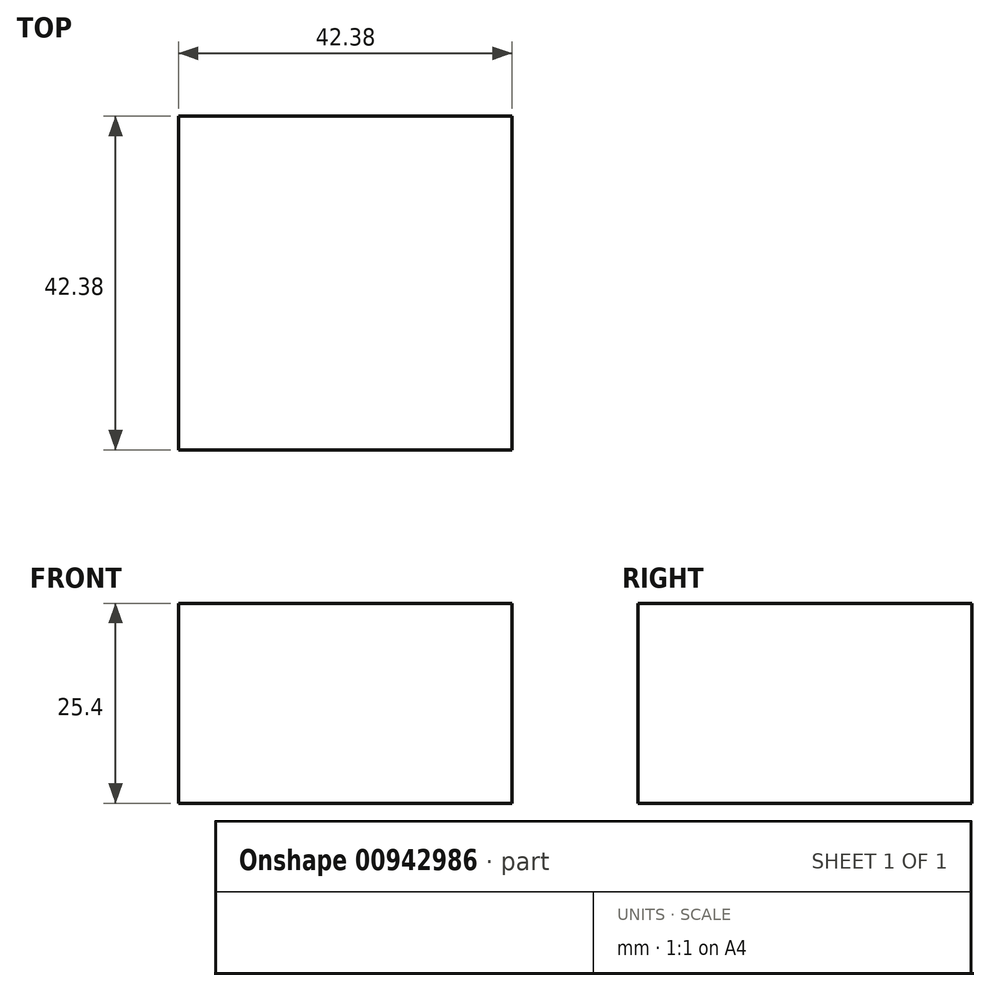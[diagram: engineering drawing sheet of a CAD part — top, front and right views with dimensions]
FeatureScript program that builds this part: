
annotation { "Feature Type Name" : "Feature", "Feature Type Description" : "" }
export const myFeature = defineFeature(function(context is Context, id is Id, definition is map)
    precondition{}
    {
        {
            var Q0;
            Q0=qCreatedBy(makeId("Top.planeOp"),FACE);
            var sketch = newSketch(context, id + "F0", { "sketchPlane" : qUnion([Q0])});
            skLineSegment(sketch, "E0.0", {"start": v(21.2, 21.2) * mm, "end": v(21.2, -21.2) * mm, "construction": true});
            skLineSegment(sketch, "E0.1", {"start": v(21.2, -21.2) * mm, "end": v(-21.2, -21.2) * mm});
            skLineSegment(sketch, "E0.2", {"start": v(-21.2, -21.2) * mm, "end": v(-21.2, 21.2) * mm});
            skLineSegment(sketch, "E0.3", {"start": v(-21.2, 21.2) * mm, "end": v(21.2, 21.2) * mm});
            skPoint(sketch, "E0.0.midPoint", {"position": v(21.2, 0) * mm});
            skLineSegment(sketch, "E1", {"start": v(21.2, -21.2) * mm, "end": v(21.2, 0) * mm});
            skLineSegment(sketch, "E2", {"start": v(21.2, 21.2) * mm, "end": v(21.2, 0) * mm});
            skLineSegment(sketch, "E3", {"start": v(0, -21.2) * mm, "end": v(-21.2, 0) * mm});
            skLineSegment(sketch, "E4", {"start": v(-21.2, 0) * mm, "end": v(0, 21.2) * mm});
            skLineSegment(sketch, "E5", {"start": v(0, 21.2) * mm, "end": v(21.2, 0) * mm});
            skLineSegment(sketch, "E6", {"start": v(21.2, 0) * mm, "end": v(0, -21.2) * mm});
            skLineSegment(sketch, "E7.top", {"start": v(-21.2, -21.2) * mm, "end": v(21.2, -21.2) * mm});
            skLineSegment(sketch, "E7.left", {"start": v(-21.2, 21.2) * mm, "end": v(-21.2, -21.2) * mm});
            skLineSegment(sketch, "E7.right", {"start": v(21.2, 21.2) * mm, "end": v(21.2, -21.2) * mm});
            skPoint(sketch, "E7.middle", {"position": v(0, 0) * mm});
            skSolve(sketch);
        }
        {
            var Q0;
            {var subQ0=sQuery(id+"F0.wireOp",EDGE,"E5");Q0=makeQuery(id+"F0.imprint","IMPRINT",FACE,{"disambiguationData":[TD([[makeQuery(id+"F0.imprint","IMPRINT",EDGE,{"derivedFrom":subQ0}),1.0]])]});}
            var Q1;
            Q1=makeQuery(id+"F0.imprint","IMPRINT",FACE,{"disambiguationData":[TD([[makeQuery(id+"F0.imprint","IMPRINT",EDGE,{"derivedFrom":sQuery(id+"F0.wireOp",EDGE,"E3")}),-1.0]])]});
            var Q2;
            {var subQ0=sQuery(id+"F0.wireOp",EDGE,"E3");Q2=makeQuery(id+"F0.imprint","IMPRINT",FACE,{"disambiguationData":[TD([[makeQuery(id+"F0.imprint","IMPRINT",EDGE,{"derivedFrom":subQ0}),1.0]])]});}
            var Q3;
            {var subQ0=sQuery(id+"F0.wireOp",EDGE,"E6");Q3=makeQuery(id+"F0.imprint","IMPRINT",FACE,{"disambiguationData":[TD([[makeQuery(id+"F0.imprint","IMPRINT",EDGE,{"derivedFrom":subQ0}),1.0]])]});}
            var Q4;
            {var subQ0=sQuery(id+"F0.wireOp",EDGE,"E4");Q4=makeQuery(id+"F0.imprint","IMPRINT",FACE,{"disambiguationData":[TD([[makeQuery(id+"F0.imprint","IMPRINT",EDGE,{"derivedFrom":subQ0}),1.0]])]});}
            extrude(context, id + "F1", {"entities" : qUnion([Q0, Q1, Q2, Q3, Q4]), "endBound" : BoundingType.SYMMETRIC, "oppositeDirection" : true, "depth" : 25.4 * mm, "offsetDistance" : 25.4 * mm});
        }
    });
